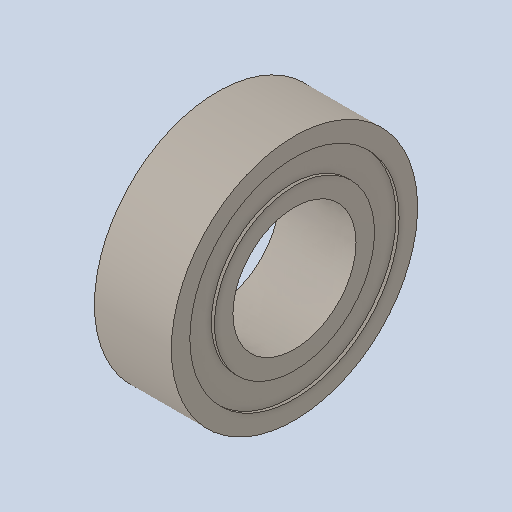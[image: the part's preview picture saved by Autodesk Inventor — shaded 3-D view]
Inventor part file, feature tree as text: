
AUTODESK INVENTOR PART (.ipt)
format: ipt  version: 2023.4 (Build 274418000, 418)  size: 127,488 bytes
history: native  units: in
note: dims shown in document units (in); Inventor stores cm internally (conversion verified against a paired STEP export)
features: revolve x1
ambient origin geometry x8: Origin, YZ Plane, XZ Plane, XY Plane, X Axis, Y Axis, Z Axis, Center Point
bodies: Solid1 (feature_tree)
feature tree (1):
  revolve  "Revolve1"  [1 undecoded]
note: 1 required parameter value undecoded (feature->parameter linkage not recoverable at this tier; creation-order binding heuristic only, values carry confidence <= 0.55)
